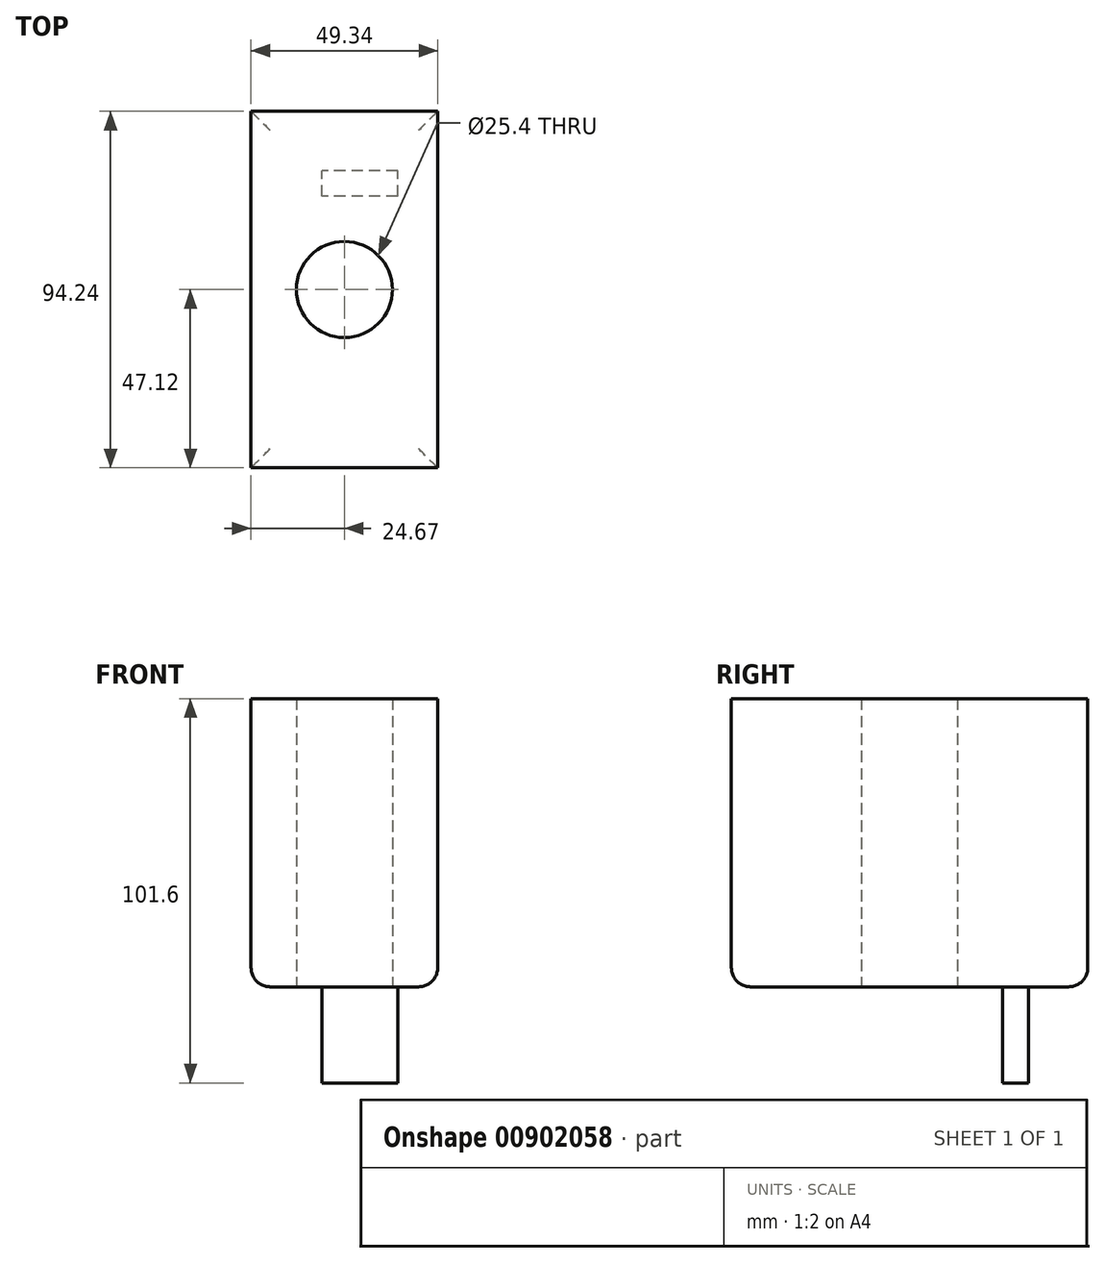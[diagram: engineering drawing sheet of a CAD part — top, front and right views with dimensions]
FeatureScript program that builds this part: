
annotation { "Feature Type Name" : "Feature", "Feature Type Description" : "" }
export const myFeature = defineFeature(function(context is Context, id is Id, definition is map)
    precondition{}
    {
        {
            var Q0;
            Q0=qCreatedBy(makeId("Top.planeOp"),FACE);
            var sketch = newSketch(context, id + "F0", { "sketchPlane" : qUnion([Q0])});
            skLineSegment(sketch, "E0.bottom", {"start": v(24.67, 47.12) * mm, "end": v(-24.67, 47.12) * mm});
            skLineSegment(sketch, "E0.top", {"start": v(24.67, -47.12) * mm, "end": v(-24.67, -47.12) * mm});
            skLineSegment(sketch, "E0.left", {"start": v(24.67, 47.12) * mm, "end": v(24.67, -47.12) * mm});
            skLineSegment(sketch, "E0.right", {"start": v(-24.67, 47.12) * mm, "end": v(-24.67, -47.12) * mm});
            skPoint(sketch, "E0.middle", {"position": v(0, 0) * mm});
            skSolve(sketch);
        }
        {
            var Q0;
            Q0=makeQuery(id+"F0.imprint","IMPRINT",FACE,{"disambiguationData":[TD([[makeQuery(id+"F0.imprint","IMPRINT",EDGE,{"derivedFrom":sQuery(id+"F0.wireOp",EDGE,"E0.bottom")}),1.0]])]});
            extrude(context, id + "F1", {"entities" : qUnion([Q0]), "depth" : 76.2 * mm, "offsetDistance" : 25.4 * mm});
        }
        {
            var Q0;
            Q0=makeQuery(id+"F1.opExtrude","CAP_FACE",FACE,{"disambiguationData":[OSD([sQuery(id+"F0.wireOp",EDGE,"E0.bottom"),sQuery(id+"F0.wireOp",EDGE,"E0.top"),sQuery(id+"F0.wireOp",EDGE,"E0.left"),sQuery(id+"F0.wireOp",EDGE,"E0.right")])],"isStart":true});
            var sketch = newSketch(context, id + "F2", { "sketchPlane" : qUnion([Q0])});
            skCircle(sketch, "E1", {"center": v(0, 0) * mm, "radius": 14.98 * mm});
            skSolve(sketch);
        }
        {
            var Q0;
            Q0=sQuery(id+"F2.wireOp",VERTEX,"E1.center");
            var Q1;
            Q1=makeQuery(id+"F1.opExtrude","SWEPT_BODY",BODY,{"disambiguationData":[OSD([sQuery(id+"F0.wireOp",EDGE,"E0.bottom"),sQuery(id+"F0.wireOp",EDGE,"E0.top"),sQuery(id+"F0.wireOp",EDGE,"E0.left"),sQuery(id+"F0.wireOp",EDGE,"E0.right")])]});
            hole(context, id + "F3", {"style" : HoleStyle.SIMPLE, "endStyle" : HoleEndStyle.THROUGH, "holeDiameter" : 25.4 * mm, "majorDiameter" : 6.35 * mm, "isTappedThrough" : true, "tappedDepth" : 12.7 * mm, "tapClearance" : 3, "locations" : qUnion([Q0]), "scope" : qUnion([Q1])});
        }
        {
            var Q0;
            Q0=makeQuery(id+"F1.opExtrude","CAP_EDGE",EDGE,{"disambiguationData":[OSD([sQuery(id+"F0.wireOp",EDGE,"E0.bottom")])],"isStart":true});
            var Q1;
            Q1=makeQuery(id+"F1.opExtrude","CAP_EDGE",EDGE,{"disambiguationData":[OSD([sQuery(id+"F0.wireOp",EDGE,"E0.right")])],"isStart":true});
            var Q2;
            Q2=makeQuery(id+"F1.opExtrude","CAP_EDGE",EDGE,{"disambiguationData":[OSD([sQuery(id+"F0.wireOp",EDGE,"E0.left")])],"isStart":true});
            var Q3;
            Q3=makeQuery(id+"F1.opExtrude","CAP_EDGE",EDGE,{"disambiguationData":[OSD([sQuery(id+"F0.wireOp",EDGE,"E0.top")])],"isStart":true});
            fillet(context, id + "F4", {"entities" : qUnion([Q0, Q1, Q2, Q3]), "radius" : 5.08 * mm, "tangentPropagation" : true, "allowEdgeOverflow" : false});
        }
        {
            var Q0;
            Q0=makeQuery(id+"F1.opExtrude","CAP_FACE",FACE,{"disambiguationData":[OSD([sQuery(id+"F0.wireOp",EDGE,"E0.bottom"),sQuery(id+"F0.wireOp",EDGE,"E0.top"),sQuery(id+"F0.wireOp",EDGE,"E0.left"),sQuery(id+"F0.wireOp",EDGE,"E0.right")])],"isStart":true});
            var sketch = newSketch(context, id + "F5", { "sketchPlane" : qUnion([Q0])});
            skLineSegment(sketch, "E2.bottom", {"start": v(14.1, -24.63) * mm, "end": v(-5.97, -24.63) * mm});
            skLineSegment(sketch, "E2.top", {"start": v(14.1, -31.4) * mm, "end": v(-5.97, -31.4) * mm});
            skLineSegment(sketch, "E2.left", {"start": v(14.1, -24.63) * mm, "end": v(14.1, -31.4) * mm});
            skLineSegment(sketch, "E2.right", {"start": v(-5.97, -24.63) * mm, "end": v(-5.97, -31.4) * mm});
            skPoint(sketch, "E2.middle", {"position": v(4.06, -28.01) * mm});
            skSolve(sketch);
        }
        {
            var Q0;
            Q0=makeQuery(id+"F5.imprint","IMPRINT",FACE,{"disambiguationData":[TD([[makeQuery(id+"F5.imprint","IMPRINT",EDGE,{"derivedFrom":sQuery(id+"F5.wireOp",EDGE,"E2.bottom")}),1.0]])]});
            extrude(context, id + "F6", {"entities" : qUnion([Q0]), "operationType" : NewBodyOperationType.ADD, "depth" : 25.4 * mm, "offsetDistance" : 25.4 * mm});
        }
    });
